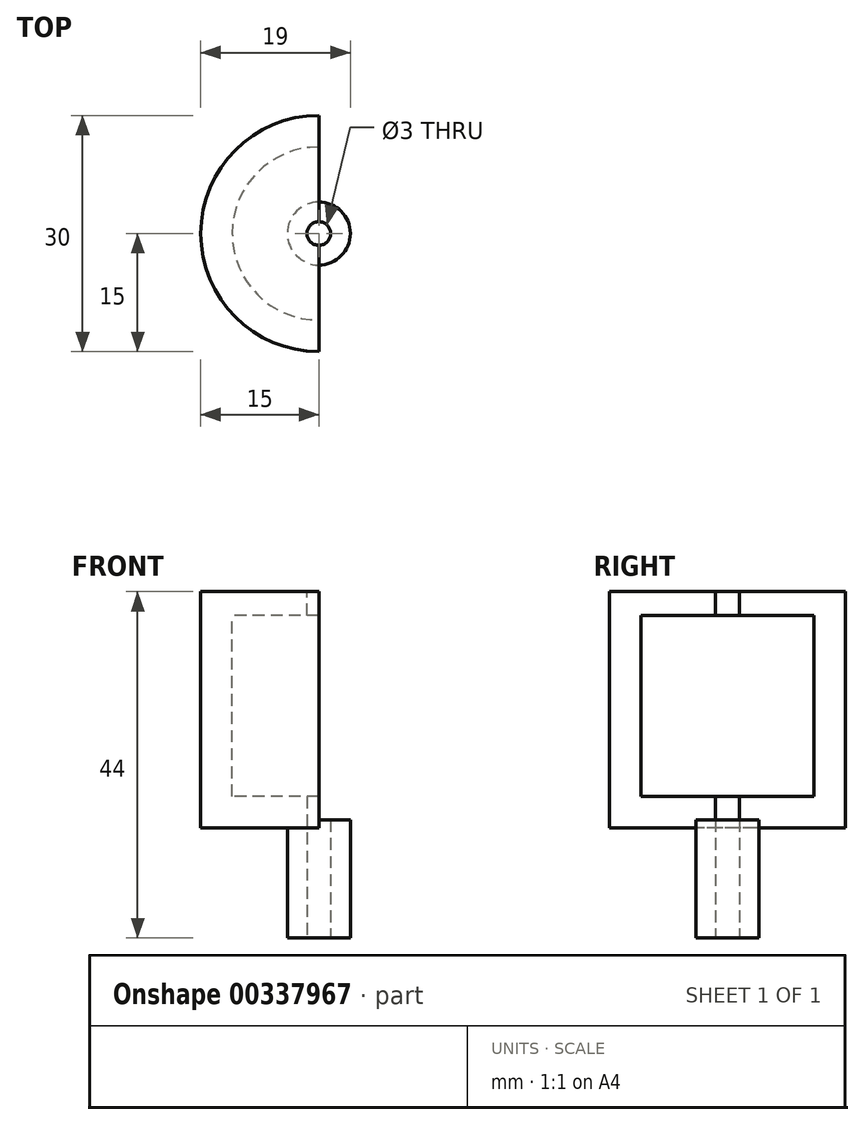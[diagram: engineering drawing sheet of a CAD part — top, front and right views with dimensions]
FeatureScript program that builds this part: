
annotation { "Feature Type Name" : "Feature", "Feature Type Description" : "" }
export const myFeature = defineFeature(function(context is Context, id is Id, definition is map)
    precondition{}
    {
        {
            var Q0;
            Q0=qCreatedBy(makeId("Top.planeOp"),FACE);
            var sketch = newSketch(context, id + "F0", { "sketchPlane" : qUnion([Q0])});
            skCircle(sketch, "E0", {"center": v(0, 0) * mm, "radius": 4 * mm});
            skCircle(sketch, "E1", {"center": v(0, 0) * mm, "radius": 1.5 * mm});
            skSolve(sketch);
        }
        {
            var Q0;
            Q0 = qSketchRegion(id + "F0", true);
            extrude(context, id + "F1", {"entities" : qUnion([Q0]), "depth" : 15 * mm});
        }
        {
            var Q0;
            Q0=qCreatedBy(makeId("Front.planeOp"),FACE);
            var sketch = newSketch(context, id + "F2", { "sketchPlane" : qUnion([Q0])});
            skLineSegment(sketch, "E2", {"start": v(0, 14) * mm, "end": v(-15, 14) * mm});
            skLineSegment(sketch, "E3", {"start": v(-15, 14) * mm, "end": v(-15, 44) * mm});
            skLineSegment(sketch, "E4", {"start": v(-15, 44) * mm, "end": v(0, 44) * mm});
            skLineSegment(sketch, "E5", {"start": v(0, 44) * mm, "end": v(0, 41) * mm});
            skLineSegment(sketch, "E6", {"start": v(0, 41) * mm, "end": v(-11, 41) * mm});
            skLineSegment(sketch, "E7", {"start": v(-11, 41) * mm, "end": v(-11, 18) * mm});
            skLineSegment(sketch, "E8", {"start": v(-11, 18) * mm, "end": v(0, 18) * mm});
            skLineSegment(sketch, "E9", {"start": v(0, 18) * mm, "end": v(0, 14) * mm});
            skLineSegment(sketch, "E10", {"start": v(0, 52.76) * mm, "end": v(0, -10.7) * mm, "construction": true});
            skPoint(sketch, "E10.endSnap0", {"position": v(0, 16) * mm});
            skSolve(sketch);
        }
        {
            var Q0;
            Q0=makeQuery(id+"F2.imprint","IMPRINT",FACE,{"disambiguationData":[TD([[makeQuery(id+"F2.imprint","IMPRINT",EDGE,{"derivedFrom":sQuery(id+"F2.wireOp",EDGE,"E2")}),-1.0]])]});
            var Q1;
            Q1=sQuery(id+"F2.wireOp",EDGE,"E10");
            revolve(context, id + "F3", {"operationType" : NewBodyOperationType.ADD, "entities" : qUnion([Q0]), "axis" : qUnion([Q1]), "revolveType" : RevolveType.SYMMETRIC, "angle" : 180 * degree});
        }
        {
            var Q0;
            Q0=makeQuery(id+"F3.opRevolve","SWEPT_FACE",FACE,{"disambiguationData":[OSD([sQuery(id+"F2.wireOp",EDGE,"E4")])]});
            var sketch = newSketch(context, id + "F4", { "sketchPlane" : qUnion([Q0])});
            skCircle(sketch, "E11", {"center": v(0, 0) * mm, "radius": 1.5 * mm});
            skSolve(sketch);
        }
        {
            var Q0;
            Q0 = qSketchRegion(id + "F4", true);
            extrude(context, id + "F5", {"entities" : qUnion([Q0]), "operationType" : NewBodyOperationType.REMOVE, "oppositeDirection" : true, "depth" : 38.1 * mm});
        }
    });
